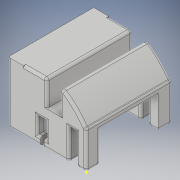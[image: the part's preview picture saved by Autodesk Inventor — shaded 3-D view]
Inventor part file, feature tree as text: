
AUTODESK INVENTOR PART (.ipt)
format: ipt  version: 2019 (Build 230136000, 136)  size: 410,624 bytes
history: native  units: in
note: dims shown in document units (in); Inventor stores cm internally (conversion verified against a paired STEP export)
features: sketch x28, fillet x6, extrude x5, other x3, plane x2
ambient origin geometry x8: Origin, YZ Plane, XZ Plane, XY Plane, X Axis, Y Axis, Z Axis, Center Point
bodies: Solid1 (feature_tree)
feature tree (44):
  other  "newShoulder.ipt"
  extrude  "Extrusion1"  Depth=1.0in TaperAngle=0.0deg
  extrude  "Extrusion2"  Depth=0.225in
  extrude  "Extrusion3"  Depth=1.0in TaperAngle=0.0deg
  fillet  "Fillet1"  Radius=0.0394in
  fillet  "Fillet3"  Radius=0.0394in
  fillet  "Fillet4"  Radius=0.0394in
  fillet  "Fillet5"  Radius=0.0394in
  sketch  "Sketch32"
  fillet  "Fillet7"  Radius=0.0394in
  extrude  "Extrusion4"  Depth=0.425in
  extrude  "Extrusion5"  Depth=0.225in TaperAngle=0.0deg
  fillet  "Fillet8"  Radius=2.0in
  other  "Solid1::newShoulder.ipt"
  other  "TaggingFeature1"
  sketch  "Sketch1"  dims[d0=0.3937in d1=1.0in d2=0.0in]
  sketch  "Sketch2"  dims[d3=0.775in d4=0.225in]
  sketch  "Sketch3"  dims[d5=1.0in d6=0.0in d7=1.0in d8=0.0in d9=0.0394in d11=0.0394in d12=0.0394in d13=0.0394in d15=0.0394in]
  sketch  "Sketch4"  dims[d16=0.0787in d17=0.425in]
  sketch  "Sketch5"  dims[d18=0.225in d19=2.0in d20=0.0in d21=2.0in d22=0.0in]
  sketch  "Sketch6"  dims[d23=0.0394in]
  sketch  "Sketch7"
  sketch  "Sketch8"
  sketch  "Sketch11"
  sketch  "Sketch12"
  sketch  "Sketch13"
  sketch  "Sketch14"
  sketch  "Sketch15"
  sketch  "Sketch17"
  sketch  "Sketch18"
  sketch  "Sketch19"
  sketch  "Sketch20"
  sketch  "Sketch21"
  sketch  "Sketch22"
  sketch  "Sketch23"
  sketch  "Sketch24"
  sketch  "Sketch30"
  plane  "Work Plane1"
  plane  "Work Plane2"
  sketch  "Sketch27"
  sketch  "Sketch28"
  sketch  "Sketch31"
  sketch  "Sketch33"
  sketch  "Sketch34"
